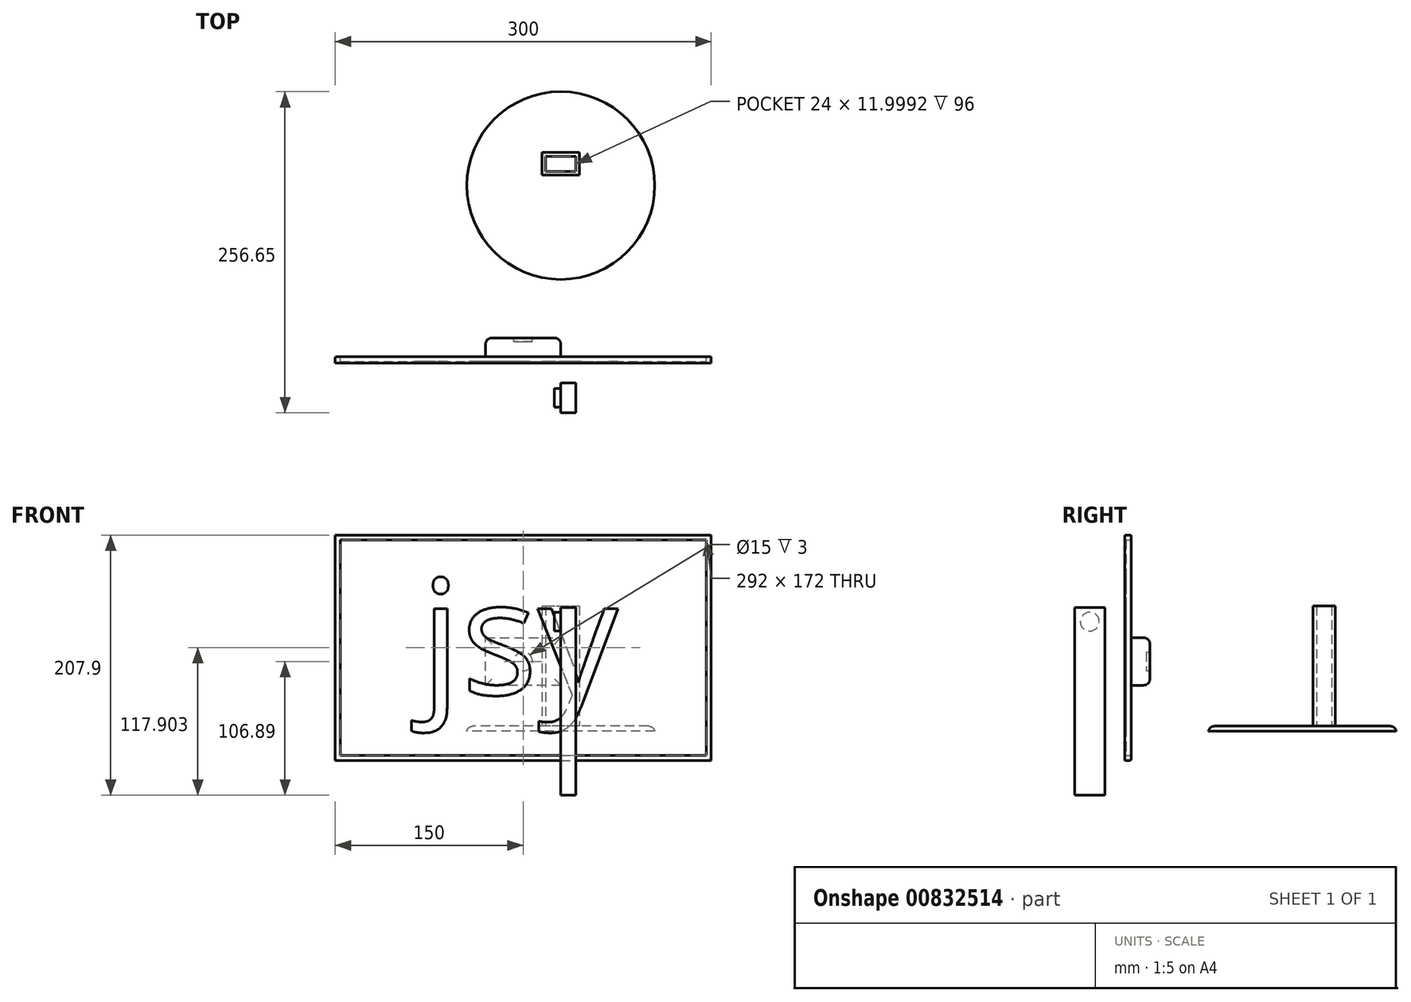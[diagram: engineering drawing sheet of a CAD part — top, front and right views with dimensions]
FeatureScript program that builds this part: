
annotation { "Feature Type Name" : "Feature", "Feature Type Description" : "" }
export const myFeature = defineFeature(function(context is Context, id is Id, definition is map)
    precondition{}
    {
        {
            var Q0;
            Q0=qCreatedBy(makeId("Front.planeOp"),FACE);
            var sketch = newSketch(context, id + "F0", { "sketchPlane" : qUnion([Q0])});
            skLineSegment(sketch, "E0.bottom", {"start": v(-180, 156.68) * mm, "end": v(120, 156.68) * mm});
            skLineSegment(sketch, "E0.top", {"start": v(-180, -23.32) * mm, "end": v(120, -23.32) * mm});
            skLineSegment(sketch, "E0.left", {"start": v(-180, 156.68) * mm, "end": v(-180, -23.32) * mm});
            skLineSegment(sketch, "E0.right", {"start": v(120, 156.68) * mm, "end": v(120, -23.32) * mm});
            skLineSegment(sketch, "E1.0", {"start": v(-176, 152.68) * mm, "end": v(116, 152.68) * mm});
            skLineSegment(sketch, "E1.1", {"start": v(-176, 152.68) * mm, "end": v(-176, -19.32) * mm});
            skLineSegment(sketch, "E1.2", {"start": v(-176, -19.32) * mm, "end": v(116, -19.32) * mm});
            skLineSegment(sketch, "E1.3", {"start": v(116, 152.68) * mm, "end": v(116, -19.32) * mm});
            skLineSegment(sketch, "E2.top", {"start": v(0, 36.68) * mm, "end": v(-60, 36.68) * mm});
            skLineSegment(sketch, "E2.left", {"start": v(0, 47.68) * mm, "end": v(0, 36.68) * mm});
            skLineSegment(sketch, "E2.right", {"start": v(-60, 47.68) * mm, "end": v(-60, 36.68) * mm});
            skPoint(sketch, "E3.end.orphan", {"position": v(-30, 36.68) * mm});
            skPoint(sketch, "E3.start.orphan", {"position": v(-30, 47.68) * mm});
            skPoint(sketch, "E4.right.end.orphan", {"position": v(85.74, 0) * mm});
            skLineSegment(sketch, "E5", {"start": v(-60, 47.68) * mm, "end": v(-60, 74.66) * mm});
            skLineSegment(sketch, "E6", {"start": v(-60, 74.66) * mm, "end": v(0, 74.66) * mm});
            skLineSegment(sketch, "E7", {"start": v(0, 74.66) * mm, "end": v(0, 47.68) * mm});
            skSolve(sketch);
        }
        {
            var Q0;
            Q0=makeQuery(id+"F0.imprint","IMPRINT",FACE,{"disambiguationData":[TD([[makeQuery(id+"F0.imprint","IMPRINT",EDGE,{"derivedFrom":sQuery(id+"F0.wireOp",EDGE,"E0.bottom")}),-1.0]])]});
            extrude(context, id + "F1", {"entities" : qUnion([Q0]), "depth" : 5 * mm, "offsetDistance" : 25 * mm});
        }
        {
            var Q0;
            Q0=makeQuery(id+"F0.imprint","IMPRINT",FACE,{"disambiguationData":[TD([[makeQuery(id+"F0.imprint","IMPRINT",EDGE,{"derivedFrom":sQuery(id+"F0.wireOp",EDGE,"E1.0")}),-1.0]])]});
            var Q1;
            Q1=makeQuery(id+"F0.imprint","IMPRINT",FACE,{"disambiguationData":[TD([[makeQuery(id+"F0.imprint","IMPRINT",EDGE,{"derivedFrom":sQuery(id+"F0.wireOp",EDGE,"E2.bottom")}),1.0]])]});
            var Q2;
            Q2=makeQuery(id+"F0.imprint","IMPRINT",FACE,{"disambiguationData":[TD([[makeQuery(id+"F0.imprint","IMPRINT",EDGE,{"derivedFrom":sQuery(id+"F0.wireOp",EDGE,"E2.top")}),-1.0]])]});
            extrude(context, id + "F2", {"entities" : qUnion([Q0, Q1, Q2]), "depth" : 4 * mm, "offsetDistance" : 25 * mm});
        }
        {
            var Q0;
            Q0=makeQuery(id+"F1.opExtrude","CAP_EDGE",EDGE,{"disambiguationData":[OSD([sQuery(id+"F0.wireOp",EDGE,"E0.top")])],"isStart":true});
            var Q1;
            Q1=makeQuery(id+"F1.opExtrude","CAP_EDGE",EDGE,{"disambiguationData":[OSD([sQuery(id+"F0.wireOp",EDGE,"E0.left")])],"isStart":true});
            var Q2;
            Q2=makeQuery(id+"F1.opExtrude","CAP_EDGE",EDGE,{"disambiguationData":[OSD([sQuery(id+"F0.wireOp",EDGE,"E0.bottom")])],"isStart":true});
            var Q3;
            Q3=makeQuery(id+"F1.opExtrude","CAP_EDGE",EDGE,{"disambiguationData":[OSD([sQuery(id+"F0.wireOp",EDGE,"E0.right")])],"isStart":true});
            var Q4;
            Q4=makeQuery(id+"FWVSXExAzP0gV0d_0.opExtrude","SWEPT_FACE",FACE,{"disambiguationData":[OSD([sQuery(id+"F0.wireOp",EDGE,"E2.right")])]});
            var Q5;
            Q5=makeQuery(id+"FWVSXExAzP0gV0d_0.opExtrude","CAP_EDGE",EDGE,{"disambiguationData":[OSD([sQuery(id+"F0.wireOp",EDGE,"E2.top")])],"isStart":false});
            var Q6;
            Q6=makeQuery(id+"FWVSXExAzP0gV0d_0.opExtrude","CAP_EDGE",EDGE,{"disambiguationData":[OSD([sQuery(id+"F0.wireOp",EDGE,"E2.top")])],"isStart":true});
            var Q7;
            Q7=makeQuery(id+"FWVSXExAzP0gV0d_0.opExtrude","CAP_FACE",FACE,{"disambiguationData":[OSD([sQuery(id+"F0.wireOp",EDGE,"E2.bottom"),sQuery(id+"F0.wireOp",EDGE,"E2.top"),sQuery(id+"F0.wireOp",EDGE,"E2.left"),sQuery(id+"F0.wireOp",EDGE,"E2.right")])],"isStart":false});
            var Q8;
            Q8=makeQuery(id+"FWVSXExAzP0gV0d_0.opExtrude","CAP_EDGE",EDGE,{"disambiguationData":[OSD([sQuery(id+"F0.wireOp",EDGE,"E2.left")])],"isStart":false});
            var Q9;
            Q9=makeQuery(id+"FWVSXExAzP0gV0d_0.opExtrude","SWEPT_FACE",FACE,{"disambiguationData":[OSD([sQuery(id+"F0.wireOp",EDGE,"E2.bottom")])]});
            var Q10;
            Q10=makeQuery(id+"FWVSXExAzP0gV0d_0.opExtrude","CAP_EDGE",EDGE,{"disambiguationData":[OSD([sQuery(id+"F0.wireOp",EDGE,"E2.left")])],"isStart":true});
            var Q11;
            Q11=makeQuery(id+"FWVSXExAzP0gV0d_0.opExtrude","SWEPT_EDGE",EDGE,{"disambiguationData":[OSD([sQuery(id+"F0.wireOp",EDGE,"E2.top"),sQuery(id+"F0.wireOp",EDGE,"E2.left")])]});
            fillet(context, id + "F3", {"entities" : qUnion([Q0, Q1, Q2, Q3, Q4, Q5, Q6, Q7, Q8, Q9, Q10, Q11]), "radius" : 1 * mm, "tangentPropagation" : true, "allowEdgeOverflow" : false});
        }
        {
            var Q0;
            Q0=qCreatedBy(makeId("Top.planeOp"),FACE);
            var sketch = newSketch(context, id + "F4", { "sketchPlane" : qUnion([Q0])});
            skCircle(sketch, "E8", {"center": v(0, 136.69) * mm, "radius": 75 * mm});
            skLineSegment(sketch, "E9", {"start": v(-15, 145.04) * mm, "end": v(-15, 163.04) * mm});
            skLineSegment(sketch, "E10", {"start": v(-15, 163.04) * mm, "end": v(15, 163.04) * mm});
            skLineSegment(sketch, "E11", {"start": v(15, 163.04) * mm, "end": v(15, 145.04) * mm});
            skPoint(sketch, "E12.start.orphan", {"position": v(0, 152.8) * mm});
            skLineSegment(sketch, "E13", {"start": v(-15, 145.04) * mm, "end": v(15, 145.04) * mm});
            skLineSegment(sketch, "E14.0", {"start": v(-12, 160.04) * mm, "end": v(12, 160.04) * mm});
            skLineSegment(sketch, "E14.1", {"start": v(-12, 148.04) * mm, "end": v(-12, 160.04) * mm});
            skLineSegment(sketch, "E14.2", {"start": v(-12, 148.04) * mm, "end": v(12, 148.04) * mm});
            skLineSegment(sketch, "E14.3", {"start": v(12, 160.04) * mm, "end": v(12, 148.04) * mm});
            skLineSegment(sketch, "E15", {"start": v(0, 160.04) * mm, "end": v(0, 152.8) * mm});
            skLineSegment(sketch, "E16.trimOffspring", {"start": v(0, 145.04) * mm, "end": v(0, 136.69) * mm});
            skPoint(sketch, "E17.orphan", {"position": v(0, 211.69) * mm});
            skSolve(sketch);
        }
        {
            var Q0;
            Q0=makeQuery(id+"F4.imprint","IMPRINT",FACE,{"disambiguationData":[TD([[makeQuery(id+"F4.imprint","IMPRINT",EDGE,{"derivedFrom":sQuery(id+"F4.wireOp",EDGE,"E9")}),-1.0]])]});
            var Q1;
            Q1=makeQuery(id+"F4.imprint","IMPRINT",FACE,{"disambiguationData":[TD([[makeQuery(id+"F4.imprint","IMPRINT",EDGE,{"derivedFrom":sQuery(id+"F4.wireOp",EDGE,"llg5yttw-F3WU-DeB2-RuAx-drhYwPVVVSWC")}),1.0]])]});
            var Q2;
            Q2=makeQuery(id+"F4.imprint","IMPRINT",FACE,{"disambiguationData":[TD([[makeQuery(id+"F4.imprint","IMPRINT",EDGE,{"derivedFrom":sQuery(id+"F4.wireOp",EDGE,"E8")}),1.0]])]});
            var Q3;
            {var subQ0=sQuery(id+"F4.wireOp",EDGE,"E14.1");Q3=makeQuery(id+"F4.imprint","IMPRINT",FACE,{"disambiguationData":[TD([[makeQuery(id+"F4.imprint","IMPRINT",EDGE,{"derivedFrom":subQ0}),-1.0]])]});}
            extrude(context, id + "F5", {"entities" : qUnion([Q0, Q1, Q2, Q3]), "depth" : 4 * mm, "offsetDistance" : 25 * mm});
        }
        {
            var Q0;
            Q0=makeQuery(id+"F4.imprint","IMPRINT",FACE,{"disambiguationData":[TD([[makeQuery(id+"F4.imprint","IMPRINT",EDGE,{"derivedFrom":sQuery(id+"F4.wireOp",EDGE,"E9")}),-1.0]])]});
            extrude(context, id + "F6", {"entities" : qUnion([Q0]), "operationType" : NewBodyOperationType.ADD, "depth" : 100 * mm, "offsetDistance" : 25 * mm});
        }
        {
            var Q0;
            Q0=makeQuery(id+"F5.opExtrude","CAP_EDGE",EDGE,{"disambiguationData":[OSD([sQuery(id+"F4.wireOp",EDGE,"E8")])],"isStart":false});
            fillet(context, id + "F7", {"entities" : qUnion([Q0]), "radius" : 5 * mm, "tangentPropagation" : true, "allowEdgeOverflow" : false});
        }
        {
            var Q0;
            Q0=qCreatedBy(makeId("Front.planeOp"),FACE);
            cPlane(context, id + "F8", {"entities" : qUnion([Q0]), "cplaneType" : CPlaneType.OFFSET, "offset" : 5 * mm, "width" : 150 * mm, "height" : 150 * mm});
        }
        {
            var Q0;
            Q0=makeQuery(id+"F0.imprint","IMPRINT",FACE,{"disambiguationData":[TD([[makeQuery(id+"F0.imprint","IMPRINT",EDGE,{"derivedFrom":sQuery(id+"F0.wireOp",EDGE,"E2.top")}),-1.0]])]});
            extrude(context, id + "F9", {"entities" : qUnion([Q0]), "operationType" : NewBodyOperationType.ADD, "oppositeDirection" : true, "depth" : 15 * mm, "offsetDistance" : 25 * mm});
        }
        {
            var Q0;
            Q0=makeQuery(id+"F9.opExtrude","CAP_FACE",FACE,{"disambiguationData":[OSD([sQuery(id+"F0.wireOp",EDGE,"E2.top"),sQuery(id+"F0.wireOp",EDGE,"E2.left"),sQuery(id+"F0.wireOp",EDGE,"E2.right"),sQuery(id+"F0.wireOp",EDGE,"E5"),sQuery(id+"F0.wireOp",EDGE,"E6"),sQuery(id+"F0.wireOp",EDGE,"E7")])],"isStart":false});
            fillet(context, id + "F10", {"entities" : qUnion([Q0]), "radius" : 5 * mm, "tangentPropagation" : true, "allowEdgeOverflow" : false});
        }
        {
            var Q0;
            Q0=qCreatedBy(makeId("Right.planeOp"),FACE);
            var sketch = newSketch(context, id + "F11", { "sketchPlane" : qUnion([Q0])});
            skLineSegment(sketch, "E18", {"start": v(-20.96, 98.78) * mm, "end": v(-20.96, -51.22) * mm});
            skLineSegment(sketch, "E19", {"start": v(-20.96, -51.22) * mm, "end": v(-44.96, -51.22) * mm});
            skLineSegment(sketch, "E20", {"start": v(-44.96, -51.22) * mm, "end": v(-44.96, 98.78) * mm});
            skLineSegment(sketch, "E21", {"start": v(-44.96, 98.78) * mm, "end": v(-20.96, 98.78) * mm});
            skCircle(sketch, "E22", {"center": v(-32.96, 87.47) * mm, "radius": 7.5 * mm});
            skPoint(sketch, "E23.trimOffspring.end.orphan", {"position": v(-44.96, 87.47) * mm});
            skPoint(sketch, "E24.start.orphan", {"position": v(-20.96, 87.47) * mm});
            skSolve(sketch);
        }
        {
            var Q0;
            Q0 = qSketchRegion(id + "F11", true);
            var Q1;
            Q1=makeQuery(id+"F11.imprint","IMPRINT",FACE,{"disambiguationData":[TD([[makeQuery(id+"F11.imprint","IMPRINT",EDGE,{"derivedFrom":sQuery(id+"F11.wireOp",EDGE,"E22")}),1.0]])]});
            extrude(context, id + "F12", {"entities" : qUnion([Q0, Q1]), "depth" : 12 * mm, "offsetDistance" : 25 * mm});
        }
        {
            var Q0;
            Q0=makeQuery(id+"F11.imprint","IMPRINT",FACE,{"disambiguationData":[TD([[makeQuery(id+"F11.imprint","IMPRINT",EDGE,{"derivedFrom":sQuery(id+"F11.wireOp",EDGE,"E22")}),1.0]])]});
            extrude(context, id + "F13", {"entities" : qUnion([Q0]), "operationType" : NewBodyOperationType.ADD, "oppositeDirection" : true, "depth" : 5 * mm, "offsetDistance" : 25 * mm});
        }
        {
            var Q0;
            Q0=makeQuery(id+"F9.opExtrude","CAP_FACE",FACE,{"disambiguationData":[OSD([sQuery(id+"F0.wireOp",EDGE,"E2.top"),sQuery(id+"F0.wireOp",EDGE,"E2.left"),sQuery(id+"F0.wireOp",EDGE,"E2.right"),sQuery(id+"F0.wireOp",EDGE,"E5"),sQuery(id+"F0.wireOp",EDGE,"E6"),sQuery(id+"F0.wireOp",EDGE,"E7")])],"isStart":false});
            var sketch = newSketch(context, id + "F14", { "sketchPlane" : qUnion([Q0])});
            skCircle(sketch, "E25", {"center": v(30, 55.67) * mm, "radius": 7.5 * mm});
            skPoint(sketch, "E26.trimOffspring.end.orphan", {"position": v(55, 55.67) * mm});
            skPoint(sketch, "E27.start.orphan", {"position": v(5, 55.67) * mm});
            skSolve(sketch);
        }
        {
            var Q0;
            Q0=makeQuery(id+"F14.imprint","IMPRINT",FACE,{"disambiguationData":[TD([[makeQuery(id+"F14.imprint","IMPRINT",EDGE,{"derivedFrom":sQuery(id+"F14.wireOp",EDGE,"E25")}),1.0]])]});
            extrude(context, id + "F15", {"entities" : qUnion([Q0]), "operationType" : NewBodyOperationType.REMOVE, "oppositeDirection" : true, "depth" : 3 * mm, "offsetDistance" : 25 * mm});
        }
        {
            var Q0;
            Q0=qCreatedBy(id+"F8.planeOp",FACE);
            var sketch = newSketch(context, id + "F16", { "sketchPlane" : qUnion([Q0])});
            skText(sketch, "E28", { "text": "jsy", "fontName": "OpenSans-Regular.ttf"});
            const initialGuessF16  = {"E28": [-0.1121, 0.02933, 1, 0, 0.0922]};
            skSetInitialGuess(sketch, initialGuessF16);
            skSolve(sketch);
        }
        {
            var Q0;
            Q0 = qSketchRegion(id + "F16", true);
            extrude(context, id + "F17", {"entities" : qUnion([Q0]), "endBound" : BoundingType.UP_TO_NEXT, "oppositeDirection" : true, "depth" : 25 * mm, "offsetDistance" : 25 * mm});
        }
    });
